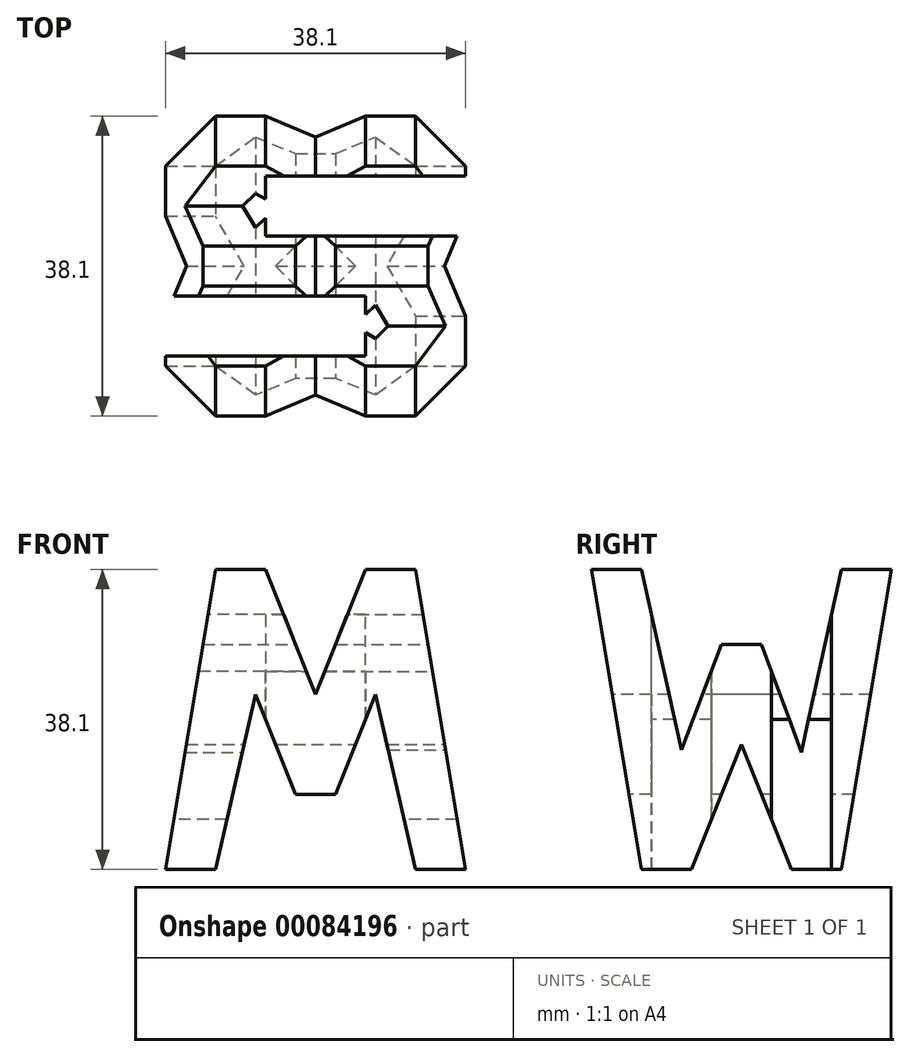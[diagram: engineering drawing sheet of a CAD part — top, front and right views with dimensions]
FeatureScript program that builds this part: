
annotation { "Feature Type Name" : "Feature", "Feature Type Description" : "" }
export const myFeature = defineFeature(function(context is Context, id is Id, definition is map)
    precondition{}
    {
        {
            var Q0;
            Q0=qCreatedBy(makeId("Front.planeOp"),FACE);
            var sketch = newSketch(context, id + "F0", { "sketchPlane" : qUnion([Q0])});
            skLineSegment(sketch, "E0", {"start": v(0, 0) * mm, "end": v(38.1, 0) * mm});
            skLineSegment(sketch, "E1", {"start": v(38.1, 0) * mm, "end": v(38.1, 38.1) * mm});
            skLineSegment(sketch, "E2", {"start": v(38.1, 38.1) * mm, "end": v(0, 38.1) * mm});
            skLineSegment(sketch, "E3", {"start": v(0, 38.1) * mm, "end": v(0, 0) * mm});
            skSolve(sketch);
        }
        {
            var Q0;
            Q0=makeQuery(id+"F0.imprint","IMPRINT",FACE,{"disambiguationData":[TD([[makeQuery(id+"F0.imprint","IMPRINT",EDGE,{"derivedFrom":sQuery(id+"F0.wireOp",EDGE,"E0")}),1.0]])]});
            extrude(context, id + "F1", {"entities" : qUnion([Q0]), "depth" : 38.1 * mm});
        }
        {
            var Q0;
            Q0=qCreatedBy(makeId("Front.planeOp"),FACE);
            cPlane(context, id + "F2", {"entities" : qUnion([Q0]), "cplaneType" : CPlaneType.OFFSET, "offset" : 38.1 * mm, "width" : 152.4 * mm, "height" : 152.4 * mm});
        }
        {
            var Q0;
            Q0=qCreatedBy(makeId("Right.planeOp"),FACE);
            cPlane(context, id + "F3", {"entities" : qUnion([Q0]), "cplaneType" : CPlaneType.OFFSET, "offset" : 38.1 * mm, "width" : 152.4 * mm, "height" : 152.4 * mm});
        }
        {
            var Q0;
            Q0=qCreatedBy(makeId("Top.planeOp"),FACE);
            cPlane(context, id + "F4", {"entities" : qUnion([Q0]), "cplaneType" : CPlaneType.OFFSET, "offset" : 38.1 * mm, "width" : 152.4 * mm, "height" : 152.4 * mm});
        }
        {
            var Q0;
            Q0=qCreatedBy(id+"F3.planeOp",FACE);
            var sketch = newSketch(context, id + "F5", { "sketchPlane" : qUnion([Q0])});
            skLineSegment(sketch, "E4", {"start": v(-38.1, 0) * mm, "end": v(0, 0) * mm});
            skLineSegment(sketch, "E5", {"start": v(-38.1, 0) * mm, "end": v(-38.1, 38.1) * mm});
            skLineSegment(sketch, "E6", {"start": v(0, 38.1) * mm, "end": v(-38.1, 38.1) * mm});
            skLineSegment(sketch, "E7", {"start": v(0, 38.1) * mm, "end": v(0, 0) * mm});
            skLineSegment(sketch, "E8", {"start": v(-38.1, 38.1) * mm, "end": v(-31.75, 0) * mm});
            skLineSegment(sketch, "E9", {"start": v(-31.75, 0) * mm, "end": v(-25.4, 0) * mm});
            skLineSegment(sketch, "E10", {"start": v(-25.4, 0) * mm, "end": v(-19.05, 15.88) * mm});
            skLineSegment(sketch, "E11", {"start": v(-19.05, 15.88) * mm, "end": v(-12.7, 0) * mm});
            skLineSegment(sketch, "E12", {"start": v(-12.7, 0) * mm, "end": v(-6.35, 0) * mm});
            skLineSegment(sketch, "E13", {"start": v(-6.35, 0) * mm, "end": v(0, 38.1) * mm});
            skLineSegment(sketch, "E14", {"start": v(-6.35, 38.1) * mm, "end": v(-11.43, 14.9) * mm});
            skLineSegment(sketch, "E15", {"start": v(-11.43, 14.9) * mm, "end": v(-16.51, 28.58) * mm});
            skLineSegment(sketch, "E16", {"start": v(-16.51, 28.58) * mm, "end": v(-21.6, 28.58) * mm});
            skLineSegment(sketch, "E17", {"start": v(-21.6, 28.58) * mm, "end": v(-26.67, 15.2) * mm});
            skLineSegment(sketch, "E18", {"start": v(-26.67, 15.2) * mm, "end": v(-31.75, 38.1) * mm});
            skLineSegment(sketch, "E19", {"start": v(-31.75, 38.1) * mm, "end": v(-38.1, 38.1) * mm});
            skSolve(sketch);
        }
        {
            var Q0;
            {var subQ0=sQuery(id+"F5.wireOp",EDGE,"E14");Q0=makeQuery(id+"F5.imprint","IMPRINT",FACE,{"disambiguationData":[TD([[makeQuery(id+"F5.imprint","IMPRINT",EDGE,{"derivedFrom":subQ0}),-1.0]])]});}
            var Q1;
            {var subQ0=sQuery(id+"F5.wireOp",EDGE,"E5");Q1=makeQuery(id+"F5.imprint","IMPRINT",FACE,{"disambiguationData":[TD([[makeQuery(id+"F5.imprint","IMPRINT",EDGE,{"derivedFrom":subQ0}),-1.0]])]});}
            var Q2;
            {var subQ0=sQuery(id+"F5.wireOp",EDGE,"E10");Q2=makeQuery(id+"F5.imprint","IMPRINT",FACE,{"disambiguationData":[TD([[makeQuery(id+"F5.imprint","IMPRINT",EDGE,{"derivedFrom":subQ0}),-1.0]])]});}
            var Q3;
            {var subQ0=sQuery(id+"F5.wireOp",EDGE,"E7");Q3=makeQuery(id+"F5.imprint","IMPRINT",FACE,{"disambiguationData":[TD([[makeQuery(id+"F5.imprint","IMPRINT",EDGE,{"derivedFrom":subQ0}),-1.0]])]});}
            extrude(context, id + "F6", {"entities" : qUnion([Q0, Q1, Q2, Q3]), "operationType" : NewBodyOperationType.REMOVE, "oppositeDirection" : true, "depth" : 38.1 * mm});
        }
        {
            var Q0;
            Q0=qCreatedBy(id+"F2.planeOp",FACE);
            var sketch = newSketch(context, id + "F7", { "sketchPlane" : qUnion([Q0])});
            skLineSegment(sketch, "E20", {"start": v(0, 38.1) * mm, "end": v(38.1, 38.1) * mm});
            skLineSegment(sketch, "E21", {"start": v(38.1, 38.1) * mm, "end": v(38.1, 0) * mm});
            skLineSegment(sketch, "E22", {"start": v(38.1, 0) * mm, "end": v(0, 0) * mm});
            skLineSegment(sketch, "E23", {"start": v(0, 0) * mm, "end": v(0, 38.1) * mm});
            skLineSegment(sketch, "E24", {"start": v(0, 0) * mm, "end": v(6.35, 38.1) * mm});
            skLineSegment(sketch, "E25", {"start": v(6.35, 38.1) * mm, "end": v(12.7, 38.1) * mm});
            skLineSegment(sketch, "E26", {"start": v(12.7, 38.1) * mm, "end": v(19.05, 22.23) * mm});
            skLineSegment(sketch, "E27", {"start": v(19.05, 22.23) * mm, "end": v(25.4, 38.1) * mm});
            skLineSegment(sketch, "E28", {"start": v(25.4, 38.1) * mm, "end": v(31.75, 38.1) * mm});
            skLineSegment(sketch, "E29", {"start": v(31.75, 38.1) * mm, "end": v(38.1, 0) * mm});
            skLineSegment(sketch, "E30", {"start": v(31.75, 0) * mm, "end": v(26.67, 22.22) * mm});
            skLineSegment(sketch, "E31", {"start": v(26.67, 22.22) * mm, "end": v(21.6, 9.52) * mm});
            skLineSegment(sketch, "E32", {"start": v(21.6, 9.53) * mm, "end": v(16.51, 9.53) * mm});
            skLineSegment(sketch, "E33", {"start": v(16.51, 9.53) * mm, "end": v(11.43, 22.23) * mm});
            skLineSegment(sketch, "E34", {"start": v(11.43, 22.23) * mm, "end": v(6.35, 0) * mm});
            skLineSegment(sketch, "E35", {"start": v(6.35, 0) * mm, "end": v(0, 0) * mm});
            skSolve(sketch);
        }
        {
            var Q0;
            {var subQ0=sQuery(id+"F7.wireOp",EDGE,"E26");Q0=makeQuery(id+"F7.imprint","IMPRINT",FACE,{"disambiguationData":[TD([[makeQuery(id+"F7.imprint","IMPRINT",EDGE,{"derivedFrom":subQ0}),1.0]])]});}
            var Q1;
            {var subQ0=sQuery(id+"F7.wireOp",EDGE,"E23");Q1=makeQuery(id+"F7.imprint","IMPRINT",FACE,{"disambiguationData":[TD([[makeQuery(id+"F7.imprint","IMPRINT",EDGE,{"derivedFrom":subQ0}),-1.0]])]});}
            var Q2;
            {var subQ2=sQuery(id+"F7.wireOp",EDGE,"E30");Q2=makeQuery(id+"F7.imprint","IMPRINT",FACE,{"disambiguationData":[TD([[makeQuery(id+"F7.imprint","IMPRINT",EDGE,{"derivedFrom":subQ2}),1.0]])]});}
            var Q3;
            {var subQ0=sQuery(id+"F7.wireOp",EDGE,"E21");Q3=makeQuery(id+"F7.imprint","IMPRINT",FACE,{"disambiguationData":[TD([[makeQuery(id+"F7.imprint","IMPRINT",EDGE,{"derivedFrom":subQ0}),-1.0]])]});}
            extrude(context, id + "F8", {"entities" : qUnion([Q0, Q1, Q2, Q3]), "operationType" : NewBodyOperationType.REMOVE, "oppositeDirection" : true, "depth" : 38.1 * mm});
        }
        {
            var Q0;
            Q0=qCreatedBy(id+"F4.planeOp",FACE);
            var sketch = newSketch(context, id + "F9", { "sketchPlane" : qUnion([Q0])});
            skLineSegment(sketch, "E36", {"start": v(0, 0) * mm, "end": v(38.1, 0) * mm});
            skLineSegment(sketch, "E37", {"start": v(38.1, 0) * mm, "end": v(38.1, -38.1) * mm});
            skLineSegment(sketch, "E38", {"start": v(38.1, -38.1) * mm, "end": v(0, -38.1) * mm});
            skLineSegment(sketch, "E39", {"start": v(0, -38.1) * mm, "end": v(0, 0) * mm});
            skLineSegment(sketch, "E40", {"start": v(38.1, -7.62) * mm, "end": v(12.7, -7.62) * mm});
            skLineSegment(sketch, "E41", {"start": v(12.7, -7.62) * mm, "end": v(12.7, -15.24) * mm});
            skLineSegment(sketch, "E42", {"start": v(12.7, -15.24) * mm, "end": v(38.1, -15.24) * mm});
            skLineSegment(sketch, "E43", {"start": v(0, -22.86) * mm, "end": v(25.4, -22.86) * mm});
            skLineSegment(sketch, "E44", {"start": v(25.4, -22.86) * mm, "end": v(25.4, -30.48) * mm});
            skLineSegment(sketch, "E45", {"start": v(25.4, -30.48) * mm, "end": v(0, -30.48) * mm});
            skSolve(sketch);
        }
        {
            var Q0;
            {var subQ0=sQuery(id+"F9.wireOp",EDGE,"E43");Q0=makeQuery(id+"F9.imprint","IMPRINT",FACE,{"disambiguationData":[TD([[makeQuery(id+"F9.imprint","IMPRINT",EDGE,{"derivedFrom":subQ0}),-1.0]])]});}
            var Q1;
            {var subQ0=sQuery(id+"F9.wireOp",EDGE,"E40");Q1=makeQuery(id+"F9.imprint","IMPRINT",FACE,{"disambiguationData":[TD([[makeQuery(id+"F9.imprint","IMPRINT",EDGE,{"derivedFrom":subQ0}),1.0]])]});}
            extrude(context, id + "F10", {"entities" : qUnion([Q0, Q1]), "operationType" : NewBodyOperationType.REMOVE, "oppositeDirection" : true, "depth" : 38.1 * mm});
        }
    });
